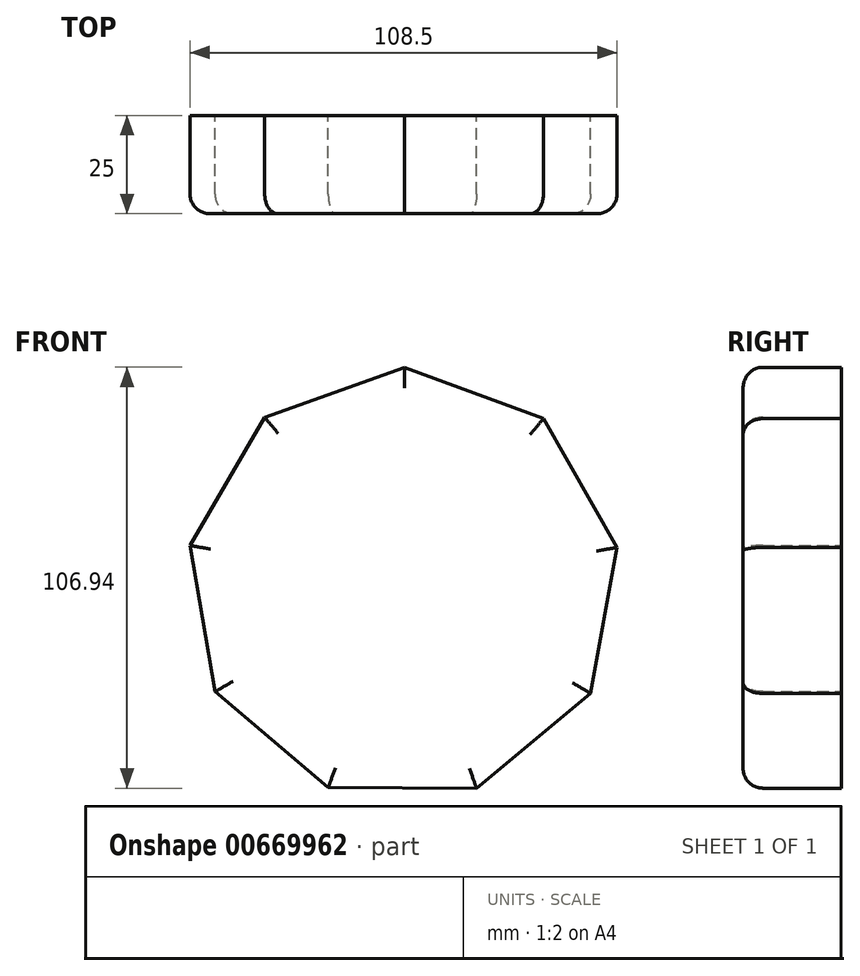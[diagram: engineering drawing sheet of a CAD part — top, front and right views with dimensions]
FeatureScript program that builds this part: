
annotation { "Feature Type Name" : "Feature", "Feature Type Description" : "" }
export const myFeature = defineFeature(function(context is Context, id is Id, definition is map)
    precondition{}
    {
        {
            var Q0;
            Q0=qCreatedBy(makeId("Front.planeOp"),FACE);
            var sketch = newSketch(context, id + "F0", { "sketchPlane" : qUnion([Q0])});
            skCircle(sketch, "E0.cCircle", {"center": v(0, 0) * mm, "radius": 55.09 * mm, "construction": true});
            skLineSegment(sketch, "E0.0", {"start": v(47.58, -27.77) * mm, "end": v(18.6, -51.85) * mm});
            skLineSegment(sketch, "E0.1", {"start": v(18.6, -51.85) * mm, "end": v(-19.09, -51.68) * mm});
            skLineSegment(sketch, "E0.2", {"start": v(-19.09, -51.68) * mm, "end": v(-47.84, -27.32) * mm});
            skLineSegment(sketch, "E0.3", {"start": v(-47.84, -27.32) * mm, "end": v(-54.2, 9.82) * mm});
            skLineSegment(sketch, "E0.4", {"start": v(-54.2, 9.82) * mm, "end": v(-35.2, 42.37) * mm});
            skLineSegment(sketch, "E0.5", {"start": v(-35.2, 42.37) * mm, "end": v(0.26, 55.09) * mm});
            skLineSegment(sketch, "E0.6", {"start": v(0.26, 55.09) * mm, "end": v(35.6, 42.03) * mm});
            skLineSegment(sketch, "E0.7", {"start": v(35.6, 42.03) * mm, "end": v(54.3, 9.3) * mm});
            skLineSegment(sketch, "E0.8", {"start": v(54.3, 9.3) * mm, "end": v(47.58, -27.77) * mm});
            skSolve(sketch);
        }
        {
            var Q0;
            Q0=makeQuery(id+"F0.imprint","IMPRINT",FACE,{"disambiguationData":[TD([[makeQuery(id+"F0.imprint","IMPRINT",EDGE,{"derivedFrom":sQuery(id+"F0.wireOp",EDGE,"E0.0")}),-1.0]])]});
            extrude(context, id + "F1", {"entities" : qUnion([Q0]), "depth" : 25 * mm, "offsetDistance" : 25 * mm});
        }
        {
            var Q0;
            Q0=makeQuery(id+"F1.opExtrude","CAP_FACE",FACE,{"disambiguationData":[OSD([sQuery(id+"F0.wireOp",EDGE,"E0.0"),sQuery(id+"F0.wireOp",EDGE,"E0.1"),sQuery(id+"F0.wireOp",EDGE,"E0.2"),sQuery(id+"F0.wireOp",EDGE,"E0.3"),sQuery(id+"F0.wireOp",EDGE,"E0.4"),sQuery(id+"F0.wireOp",EDGE,"E0.5"),sQuery(id+"F0.wireOp",EDGE,"E0.6"),sQuery(id+"F0.wireOp",EDGE,"E0.7"),sQuery(id+"F0.wireOp",EDGE,"E0.8")])],"isStart":false});
            fillet(context, id + "F2", {"entities" : qUnion([Q0]), "radius" : 5 * mm, "tangentPropagation" : true, "allowEdgeOverflow" : false});
        }
    });
